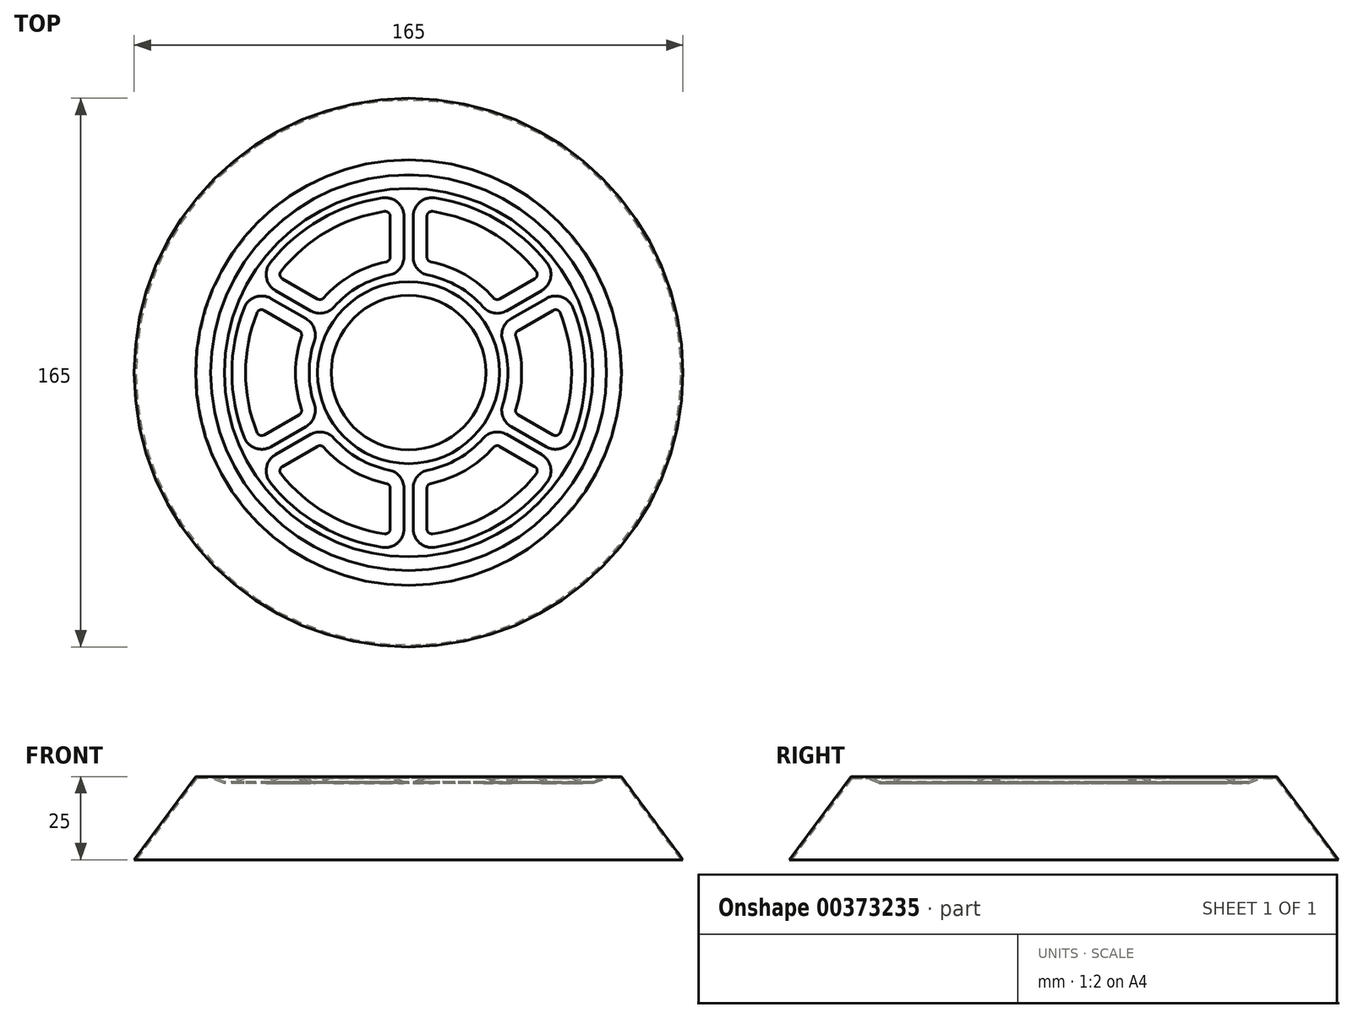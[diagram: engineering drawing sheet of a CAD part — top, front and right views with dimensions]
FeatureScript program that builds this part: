
annotation { "Feature Type Name" : "Feature", "Feature Type Description" : "" }
export const myFeature = defineFeature(function(context is Context, id is Id, definition is map)
    precondition{}
    {
        {
            var Q0;
            Q0=qCreatedBy(makeId("Top.planeOp"),FACE);
            var sketch = newSketch(context, id + "F0", { "sketchPlane" : qUnion([Q0])});
            skCircle(sketch, "E0", {"center": v(0, 0) * mm, "radius": 64 * mm});
            skSolve(sketch);
        }
        {
            var Q0;
            Q0=qCreatedBy(makeId("Top.planeOp"),FACE);
            cPlane(context, id + "F1", {"entities" : qUnion([Q0]), "cplaneType" : CPlaneType.OFFSET, "offset" : 25 * mm, "oppositeDirection" : true, "width" : 150 * mm, "height" : 150 * mm});
        }
        {
            var Q0;
            Q0=qCreatedBy(id+"F1.planeOp",FACE);
            var sketch = newSketch(context, id + "F2", { "sketchPlane" : qUnion([Q0])});
            skCircle(sketch, "E1", {"center": v(0, 0) * mm, "radius": 82.5 * mm});
            skSolve(sketch);
        }
        {
            var Q0;
            Q0=makeQuery(id+"F0.imprint","IMPRINT",FACE,{"disambiguationData":[TD([[makeQuery(id+"F0.imprint","IMPRINT",EDGE,{"derivedFrom":sQuery(id+"F0.wireOp",EDGE,"E0")}),1.0]])]});
            var Q1;
            Q1=makeQuery(id+"F2.imprint","IMPRINT",FACE,{"disambiguationData":[TD([[makeQuery(id+"F2.imprint","IMPRINT",EDGE,{"derivedFrom":sQuery(id+"F2.wireOp",EDGE,"E1")}),1.0]])]});
            var Q2;
            Q2=sQuery(id+"F0.wireOp",EDGE,"E0");
            var Q3;
            Q3=sQuery(id+"F2.wireOp",EDGE,"E1");
            loft(context, id + "F3", {"sheetProfilesArray" : [{ "sheetProfileEntities" : qUnion([Q0]) }, { "sheetProfileEntities" : qUnion([Q1]) }], "wireProfilesArray" : [{ "wireProfileEntities" : qUnion([Q2]) }, { "wireProfileEntities" : qUnion([Q3]) }]});
        }
        {
            var Q0;
            Q0=makeQuery(id+"F3.opLoft","CAP_FACE",FACE,{"disambiguationData":[OSD([makeQuery(id+"F0.imprint","IMPRINT",FACE,{"disambiguationData":[TD([[makeQuery(id+"F0.imprint","IMPRINT",EDGE,{"derivedFrom":sQuery(id+"F0.wireOp",EDGE,"E0")}),1.0]])]})])],"isStart":true});
            var sketch = newSketch(context, id + "F4", { "sketchPlane" : qUnion([Q0])});
            skCircle(sketch, "E2", {"center": v(0, 0) * mm, "radius": 59.5 * mm});
            skCircle(sketch, "E3", {"center": v(0, 0) * mm, "radius": 23.25 * mm});
            skArc(sketch, "E4", {"start": v(-7.22, 48.47) * mm, "mid": v(-24.5, 42.44) * mm, "end": v(-38.36, 30.49) * mm});
            skArc(sketch, "E5", {"start": v(-6.7, 33.33) * mm, "mid": v(-17, 29.44) * mm, "end": v(-25.51, 22.47) * mm});
            skLineSegment(sketch, "E6", {"start": v(0, 59.5) * mm, "end": v(0, 0) * mm});
            skLineSegment(sketch, "E7", {"start": v(-5.5, 46.98) * mm, "end": v(-5.5, 34.8) * mm});
            skLineSegment(sketch, "E8", {"start": v(0, 0) * mm, "end": v(-42.44, 24.5) * mm});
            skLineSegment(sketch, "E9", {"start": v(-27.4, 22.16) * mm, "end": v(-37.94, 28.25) * mm});
            skPoint(sketch, "E10.visualSharp", {"position": v(-5.5, 48.7) * mm});
            skArc(sketch, "E10.filletArc", {"start": v(-5.5, 46.98) * mm, "mid": v(-6.02, 48.12) * mm, "end": v(-7.22, 48.47) * mm});
            skPoint(sketch, "E11.visualSharp", {"position": v(-5.5, 33.55) * mm});
            skArc(sketch, "E11.filletArc", {"start": v(-6.7, 33.33) * mm, "mid": v(-5.84, 33.85) * mm, "end": v(-5.5, 34.8) * mm});
            skPoint(sketch, "E12.visualSharp", {"position": v(-26.3, 21.54) * mm});
            skArc(sketch, "E12.filletArc", {"start": v(-27.4, 22.16) * mm, "mid": v(-26.4, 21.98) * mm, "end": v(-25.51, 22.47) * mm});
            skPoint(sketch, "E13.visualSharp", {"position": v(-39.42, 29.1) * mm});
            skArc(sketch, "E13.filletArc", {"start": v(-38.36, 30.49) * mm, "mid": v(-38.66, 29.27) * mm, "end": v(-37.94, 28.25) * mm});
            skArc(sketch, "E14.1.0", {"start": v(-45.58, 17.98) * mm, "mid": v(-49, 0) * mm, "end": v(-45.58, -17.98) * mm});
            skArc(sketch, "E14.1.1", {"start": v(-32.22, 10.86) * mm, "mid": v(-34, 0) * mm, "end": v(-32.22, -10.86) * mm});
            skPoint(sketch, "E14.1.2", {"position": v(-44.92, 19.58) * mm});
            skArc(sketch, "E14.1.3", {"start": v(-43.44, 18.73) * mm, "mid": v(-44.68, 18.84) * mm, "end": v(-45.58, 17.98) * mm});
            skLineSegment(sketch, "E14.1.4", {"start": v(-43.44, 18.73) * mm, "end": v(-32.9, 12.64) * mm});
            skArc(sketch, "E14.1.5", {"start": v(-32.22, 10.86) * mm, "mid": v(-32.24, 11.87) * mm, "end": v(-32.9, 12.64) * mm});
            skPoint(sketch, "E14.1.6", {"position": v(-31.8, -12.01) * mm});
            skArc(sketch, "E14.1.7", {"start": v(-32.9, -12.64) * mm, "mid": v(-32.24, -11.87) * mm, "end": v(-32.22, -10.86) * mm});
            skLineSegment(sketch, "E14.1.8", {"start": v(-32.9, -12.64) * mm, "end": v(-43.44, -18.73) * mm});
            skArc(sketch, "E14.1.9", {"start": v(-45.58, -17.98) * mm, "mid": v(-44.68, -18.84) * mm, "end": v(-43.44, -18.73) * mm});
            skArc(sketch, "E14.2.0", {"start": v(-38.36, -30.49) * mm, "mid": v(-24.5, -42.44) * mm, "end": v(-7.22, -48.47) * mm});
            skArc(sketch, "E14.2.1", {"start": v(-25.51, -22.47) * mm, "mid": v(-17, -29.44) * mm, "end": v(-6.7, -33.33) * mm});
            skPoint(sketch, "E14.2.2", {"position": v(-39.42, -29.1) * mm});
            skArc(sketch, "E14.2.3", {"start": v(-37.94, -28.25) * mm, "mid": v(-38.66, -29.27) * mm, "end": v(-38.36, -30.49) * mm});
            skLineSegment(sketch, "E14.2.4", {"start": v(-37.94, -28.25) * mm, "end": v(-27.4, -22.16) * mm});
            skArc(sketch, "E14.2.5", {"start": v(-25.51, -22.47) * mm, "mid": v(-26.4, -21.98) * mm, "end": v(-27.4, -22.16) * mm});
            skPoint(sketch, "E14.2.6", {"position": v(-5.5, -33.55) * mm});
            skArc(sketch, "E14.2.7", {"start": v(-5.5, -34.8) * mm, "mid": v(-5.84, -33.85) * mm, "end": v(-6.7, -33.33) * mm});
            skLineSegment(sketch, "E14.2.8", {"start": v(-5.5, -34.8) * mm, "end": v(-5.5, -46.98) * mm});
            skArc(sketch, "E14.2.9", {"start": v(-7.22, -48.47) * mm, "mid": v(-6.02, -48.12) * mm, "end": v(-5.5, -46.98) * mm});
            skArc(sketch, "E14.3.0", {"start": v(7.22, -48.47) * mm, "mid": v(24.5, -42.44) * mm, "end": v(38.36, -30.49) * mm});
            skArc(sketch, "E14.3.1", {"start": v(6.7, -33.33) * mm, "mid": v(17, -29.44) * mm, "end": v(25.51, -22.47) * mm});
            skPoint(sketch, "E14.3.2", {"position": v(5.5, -48.7) * mm});
            skArc(sketch, "E14.3.3", {"start": v(5.5, -46.98) * mm, "mid": v(6.02, -48.12) * mm, "end": v(7.22, -48.47) * mm});
            skLineSegment(sketch, "E14.3.4", {"start": v(5.5, -46.98) * mm, "end": v(5.5, -34.8) * mm});
            skArc(sketch, "E14.3.5", {"start": v(6.7, -33.33) * mm, "mid": v(5.84, -33.85) * mm, "end": v(5.5, -34.8) * mm});
            skPoint(sketch, "E14.3.6", {"position": v(26.3, -21.54) * mm});
            skArc(sketch, "E14.3.7", {"start": v(27.4, -22.16) * mm, "mid": v(26.4, -21.98) * mm, "end": v(25.51, -22.47) * mm});
            skLineSegment(sketch, "E14.3.8", {"start": v(27.4, -22.16) * mm, "end": v(37.94, -28.25) * mm});
            skArc(sketch, "E14.3.9", {"start": v(38.36, -30.49) * mm, "mid": v(38.66, -29.27) * mm, "end": v(37.94, -28.25) * mm});
            skArc(sketch, "E14.4.0", {"start": v(45.58, -17.98) * mm, "mid": v(49, 0) * mm, "end": v(45.58, 17.98) * mm});
            skArc(sketch, "E14.4.1", {"start": v(32.22, -10.86) * mm, "mid": v(34, 0) * mm, "end": v(32.22, 10.86) * mm});
            skPoint(sketch, "E14.4.2", {"position": v(44.92, -19.58) * mm});
            skArc(sketch, "E14.4.3", {"start": v(43.44, -18.73) * mm, "mid": v(44.68, -18.84) * mm, "end": v(45.58, -17.98) * mm});
            skLineSegment(sketch, "E14.4.4", {"start": v(43.44, -18.73) * mm, "end": v(32.9, -12.64) * mm});
            skArc(sketch, "E14.4.5", {"start": v(32.22, -10.86) * mm, "mid": v(32.24, -11.87) * mm, "end": v(32.9, -12.64) * mm});
            skPoint(sketch, "E14.4.6", {"position": v(31.8, 12.01) * mm});
            skArc(sketch, "E14.4.7", {"start": v(32.9, 12.64) * mm, "mid": v(32.24, 11.87) * mm, "end": v(32.22, 10.86) * mm});
            skLineSegment(sketch, "E14.4.8", {"start": v(32.9, 12.64) * mm, "end": v(43.44, 18.73) * mm});
            skArc(sketch, "E14.4.9", {"start": v(45.58, 17.98) * mm, "mid": v(44.68, 18.84) * mm, "end": v(43.44, 18.73) * mm});
            skArc(sketch, "E14.5.0", {"start": v(38.36, 30.49) * mm, "mid": v(24.5, 42.44) * mm, "end": v(7.22, 48.47) * mm});
            skArc(sketch, "E14.5.1", {"start": v(25.51, 22.47) * mm, "mid": v(17, 29.44) * mm, "end": v(6.7, 33.33) * mm});
            skPoint(sketch, "E14.5.2", {"position": v(39.42, 29.1) * mm});
            skArc(sketch, "E14.5.3", {"start": v(37.94, 28.25) * mm, "mid": v(38.66, 29.27) * mm, "end": v(38.36, 30.49) * mm});
            skLineSegment(sketch, "E14.5.4", {"start": v(37.94, 28.25) * mm, "end": v(27.4, 22.16) * mm});
            skArc(sketch, "E14.5.5", {"start": v(25.51, 22.47) * mm, "mid": v(26.4, 21.98) * mm, "end": v(27.4, 22.16) * mm});
            skPoint(sketch, "E14.5.6", {"position": v(5.5, 33.55) * mm});
            skArc(sketch, "E14.5.7", {"start": v(5.5, 34.8) * mm, "mid": v(5.84, 33.85) * mm, "end": v(6.7, 33.33) * mm});
            skLineSegment(sketch, "E14.5.8", {"start": v(5.5, 34.8) * mm, "end": v(5.5, 46.98) * mm});
            skArc(sketch, "E14.5.9", {"start": v(7.22, 48.47) * mm, "mid": v(6.02, 48.12) * mm, "end": v(5.5, 46.98) * mm});
            skSolve(sketch);
        }
        {
            var Q0;
            Q0=makeQuery(id+"F4.imprint","IMPRINT",FACE,{"disambiguationData":[TD([[makeQuery(id+"F4.imprint","IMPRINT",EDGE,{"derivedFrom":sQuery(id+"F4.wireOp",EDGE,"E2")}),1.0]])]});
            extrude(context, id + "F5", {"entities" : qUnion([Q0]), "operationType" : NewBodyOperationType.REMOVE, "oppositeDirection" : true, "depth" : 1.5 * mm, "hasDraft" : true, "draftAngle" : 70 * degree, "draftPullDirection" : true});
        }
        {
            var Q0;
            Q0=makeQuery(id+"F3.opLoft","CAP_FACE",FACE,{"disambiguationData":[OSD([makeQuery(id+"F2.imprint","IMPRINT",FACE,{"disambiguationData":[TD([[makeQuery(id+"F2.imprint","IMPRINT",EDGE,{"derivedFrom":sQuery(id+"F2.wireOp",EDGE,"E1")}),1.0]])]})])],"isStart":true});
            shell(context, id + "F6", {"entities" : qUnion([Q0]), "thickness" : 0.5 * mm});
        }
    });
